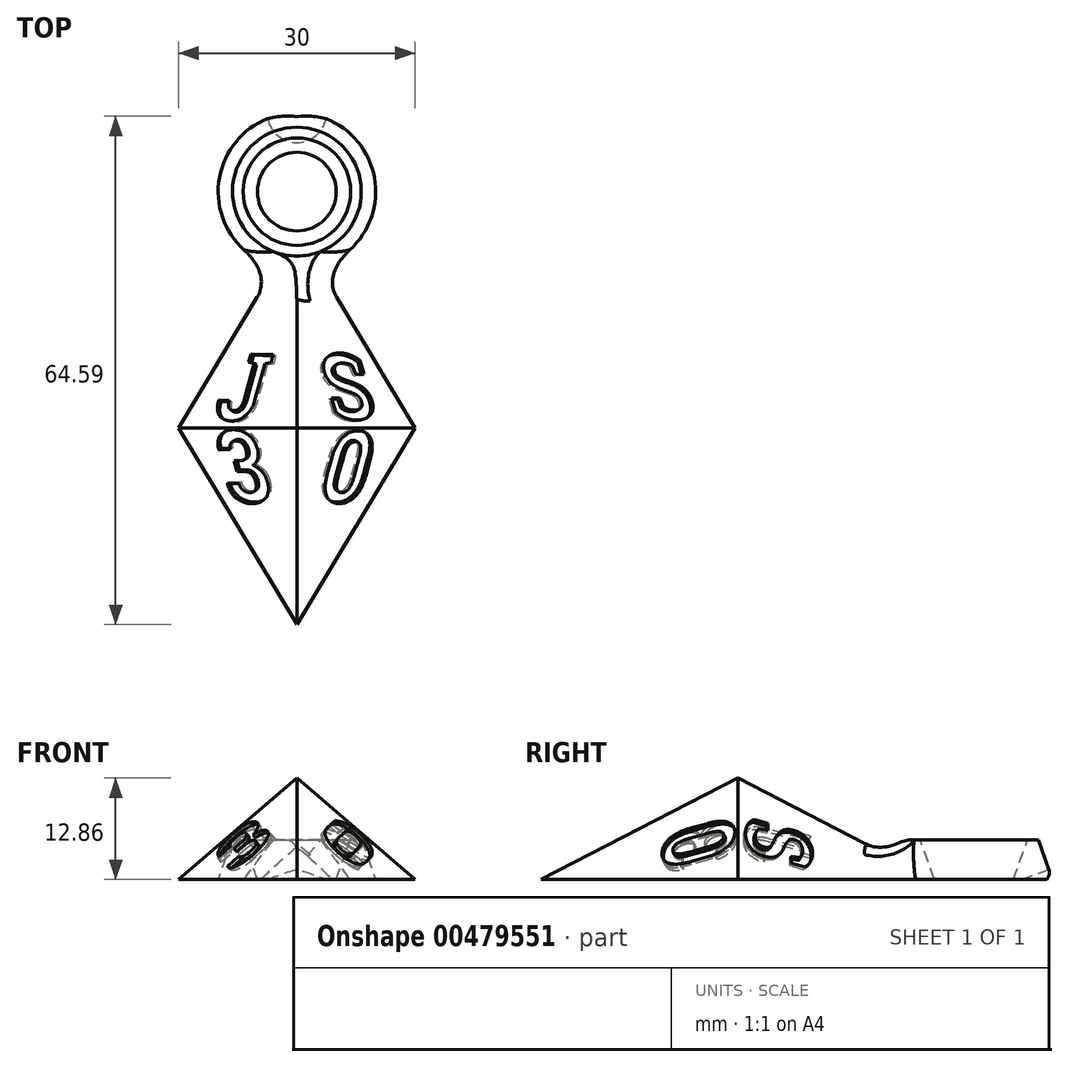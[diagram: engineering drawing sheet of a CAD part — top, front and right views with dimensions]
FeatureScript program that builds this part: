
annotation { "Feature Type Name" : "Feature", "Feature Type Description" : "" }
export const myFeature = defineFeature(function(context is Context, id is Id, definition is map)
    precondition{}
    {
        {
            var Q0;
            Q0=qCreatedBy(makeId("Top.planeOp"),FACE);
            var sketch = newSketch(context, id + "F0", { "sketchPlane" : qUnion([Q0])});
            skLineSegment(sketch, "E0", {"start": v(-15, 0) * mm, "end": v(0, 25) * mm});
            skLineSegment(sketch, "E1", {"start": v(0, 25) * mm, "end": v(0, 0) * mm, "construction": true});
            skLineSegment(sketch, "E2", {"start": v(0, 0) * mm, "end": v(0, -25) * mm, "construction": true});
            skLineSegment(sketch, "E3", {"start": v(0, -25) * mm, "end": v(-15, 0) * mm});
            skLineSegment(sketch, "E4.MirrorCS", {"start": v(15, 0) * mm, "end": v(0, 25) * mm});
            skLineSegment(sketch, "E5.MirrorCS", {"start": v(0, -25) * mm, "end": v(15, 0) * mm});
            skSolve(sketch);
        }
        {
            var Q0;
            Q0=makeQuery(id+"F0.imprint","IMPRINT",FACE,{"disambiguationData":[TD([[makeQuery(id+"F0.imprint","IMPRINT",EDGE,{"derivedFrom":sQuery(id+"F0.wireOp",EDGE,"E0")}),-1.0]])]});
            extrude(context, id + "F1", {"entities" : qUnion([Q0]), "depth" : 25.4 * mm, "hasDraft" : true, "draftAngle" : 45 * degree, "draftPullDirection" : true});
        }
        {
            var Q0;
            Q0=makeQuery(id+"F1.opExtrude","SWEPT_FACE",FACE,{"disambiguationData":[OSD([sQuery(id+"F0.wireOp",EDGE,"E0")])]});
            var sketch = newSketch(context, id + "F2", { "sketchPlane" : qUnion([Q0])});
            skText(sketch, "E6", { "text": "J", "fontName": "RobotoSlab-Bold.ttf"});
            skLineSegment(sketch, "E7.0", {"start": v(-11.93, 0) * mm, "end": v(6.93, 22.23) * mm});
            const initialGuessF2  = {"E6": [-0.0066, -0.00045, 0.94694, -0.3214, 0.00914]};
            skSetInitialGuess(sketch, initialGuessF2);
            skSolve(sketch);
        }
        {
            var Q0;
            Q0 = qSketchRegion(id + "F2", true);
            extrude(context, id + "F3", {"entities" : qUnion([Q0]), "operationType" : NewBodyOperationType.REMOVE, "oppositeDirection" : true, "depth" : .5 * mm});
        }
        {
            var Q0;
            Q0=makeQuery(id+"F1.opExtrude","SWEPT_FACE",FACE,{"disambiguationData":[OSD([sQuery(id+"F0.wireOp",EDGE,"E4.MirrorCS")])]});
            var sketch = newSketch(context, id + "F4", { "sketchPlane" : qUnion([Q0])});
            skText(sketch, "E8", { "text": "S", "fontName": "RobotoSlab-Bold.ttf"});
            skLineSegment(sketch, "E9.0", {"start": v(11.93, 0) * mm, "end": v(-6.93, 22.23) * mm});
            const initialGuessF4  = {"E8": [-0.00101, -0.0029, 0.94694, 0.3214, 0.00902]};
            skSetInitialGuess(sketch, initialGuessF4);
            skSolve(sketch);
        }
        {
            var Q0;
            Q0 = qSketchRegion(id + "F4", true);
            extrude(context, id + "F5", {"entities" : qUnion([Q0]), "operationType" : NewBodyOperationType.REMOVE, "oppositeDirection" : true, "depth" : .5 * mm});
        }
        {
            var Q0;
            Q0=makeQuery(id+"F1.opExtrude","SWEPT_FACE",FACE,{"disambiguationData":[OSD([sQuery(id+"F0.wireOp",EDGE,"E3")])]});
            var sketch = newSketch(context, id + "F6", { "sketchPlane" : qUnion([Q0])});
            skText(sketch, "E10", { "text": "3", "fontName": "RobotoSlab-Bold.ttf"});
            const initialGuessF6  = {"E10": [-0.00367, -0.0082, 0.94694, 0.3214, 0.00992]};
            skSetInitialGuess(sketch, initialGuessF6);
            skSolve(sketch);
        }
        {
            var Q0;
            Q0 = qSketchRegion(id + "F6", true);
            extrude(context, id + "F7", {"entities" : qUnion([Q0]), "operationType" : NewBodyOperationType.REMOVE, "oppositeDirection" : true, "depth" : .5 * mm});
        }
        {
            var Q0;
            Q0=makeQuery(id+"F1.opExtrude","SWEPT_FACE",FACE,{"disambiguationData":[OSD([sQuery(id+"F0.wireOp",EDGE,"E5.MirrorCS")])]});
            var sketch = newSketch(context, id + "F8", { "sketchPlane" : qUnion([Q0])});
            skText(sketch, "E11", { "text": "0", "fontName": "RobotoSlab-Bold.ttf"});
            skLineSegment(sketch, "E12.0", {"start": v(-6.93, -22.23) * mm, "end": v(11.93, 0) * mm});
            const initialGuessF8  = {"E11": [-0.00391, -0.00563, 0.94694, -0.3214, 0.00977]};
            skSetInitialGuess(sketch, initialGuessF8);
            skSolve(sketch);
        }
        {
            var Q0;
            Q0 = qSketchRegion(id + "F8", true);
            extrude(context, id + "F9", {"entities" : qUnion([Q0]), "operationType" : NewBodyOperationType.REMOVE, "oppositeDirection" : true, "depth" : .5 * mm});
        }
        {
            var Q0;
            Q0=makeQuery(id+"F1.opExtrude","CAP_FACE",FACE,{"disambiguationData":[OSD([sQuery(id+"F0.wireOp",EDGE,"E0"),sQuery(id+"F0.wireOp",EDGE,"E3"),sQuery(id+"F0.wireOp",EDGE,"E4.MirrorCS"),sQuery(id+"F0.wireOp",EDGE,"E5.MirrorCS")])],"isStart":true});
            var sketch = newSketch(context, id + "F10", { "sketchPlane" : qUnion([Q0])});
            skCircle(sketch, "E13", {"center": v(0, -30) * mm, "radius": 10 * mm});
            skCircle(sketch, "E14", {"center": v(0, -30) * mm, "radius": 5 * mm});
            skSolve(sketch);
        }
        {
            var Q0;
            Q0 = qSketchRegion(id + "F10", true);
            extrude(context, id + "F11", {"entities" : qUnion([Q0]), "operationType" : NewBodyOperationType.ADD, "oppositeDirection" : true, "depth" : 5 * mm, "hasDraft" : true, "draftAngle" : 20 * degree, "draftPullDirection" : true});
        }
        {
            var Q0;
            Q0=makeQuery(id+"F11.boolean.opBoolean","INTERSECT",EDGE,{"derivedFrom":[makeQuery(id+"F1.opExtrude","SWEPT_FACE",FACE,{"disambiguationData":[OSD([sQuery(id+"F0.wireOp",EDGE,"E0")])]}),makeQuery(id+"F11.opExtrude","SWEPT_FACE",FACE,{"disambiguationData":[OSD([sQuery(id+"F10.wireOp",EDGE,"E13")])]})]});
            var Q1;
            Q1=makeQuery(id+"F11.boolean.opBoolean","INTERSECT",EDGE,{"derivedFrom":[makeQuery(id+"F1.opExtrude","SWEPT_FACE",FACE,{"disambiguationData":[OSD([sQuery(id+"F0.wireOp",EDGE,"E4.MirrorCS")])]}),makeQuery(id+"F11.opExtrude","SWEPT_FACE",FACE,{"disambiguationData":[OSD([sQuery(id+"F10.wireOp",EDGE,"E13")])]})]});
            fillet(context, id + "F12", {"entities" : qUnion([Q0, Q1]), "radius" : 5.08 * mm, "tangentPropagation" : true, "allowEdgeOverflow" : false});
        }
        {
            var Q0;
            Q0=makeQuery(id+"F11.boolean.opBoolean","MERGE",FACE,{"derivedFrom":[makeQuery(id+"F1.opExtrude","CAP_FACE",FACE,{"disambiguationData":[OSD([sQuery(id+"F0.wireOp",EDGE,"E0"),sQuery(id+"F0.wireOp",EDGE,"E3"),sQuery(id+"F0.wireOp",EDGE,"E4.MirrorCS"),sQuery(id+"F0.wireOp",EDGE,"E5.MirrorCS")])],"isStart":true}),makeQuery(id+"F11.opExtrude","CAP_FACE",FACE,{"disambiguationData":[OSD([sQuery(id+"F10.wireOp",EDGE,"E13"),sQuery(id+"F10.wireOp",EDGE,"E14")])],"isStart":true})]});
            var sketch = newSketch(context, id + "F13", { "sketchPlane" : qUnion([Q0])});
            skCircle(sketch, "E15", {"center": v(0, -40) * mm, "radius": 3.77 * mm});
            skSolve(sketch);
        }
        {
            var Q0;
            Q0 = qSketchRegion(id + "F13", true);
            extrude(context, id + "F14", {"entities" : qUnion([Q0]), "operationType" : NewBodyOperationType.REMOVE, "oppositeDirection" : true, "depth" : 25.4 * mm, "hasDraft" : true, "draftAngle" : 70 * degree, "draftPullDirection" : true});
        }
    });
